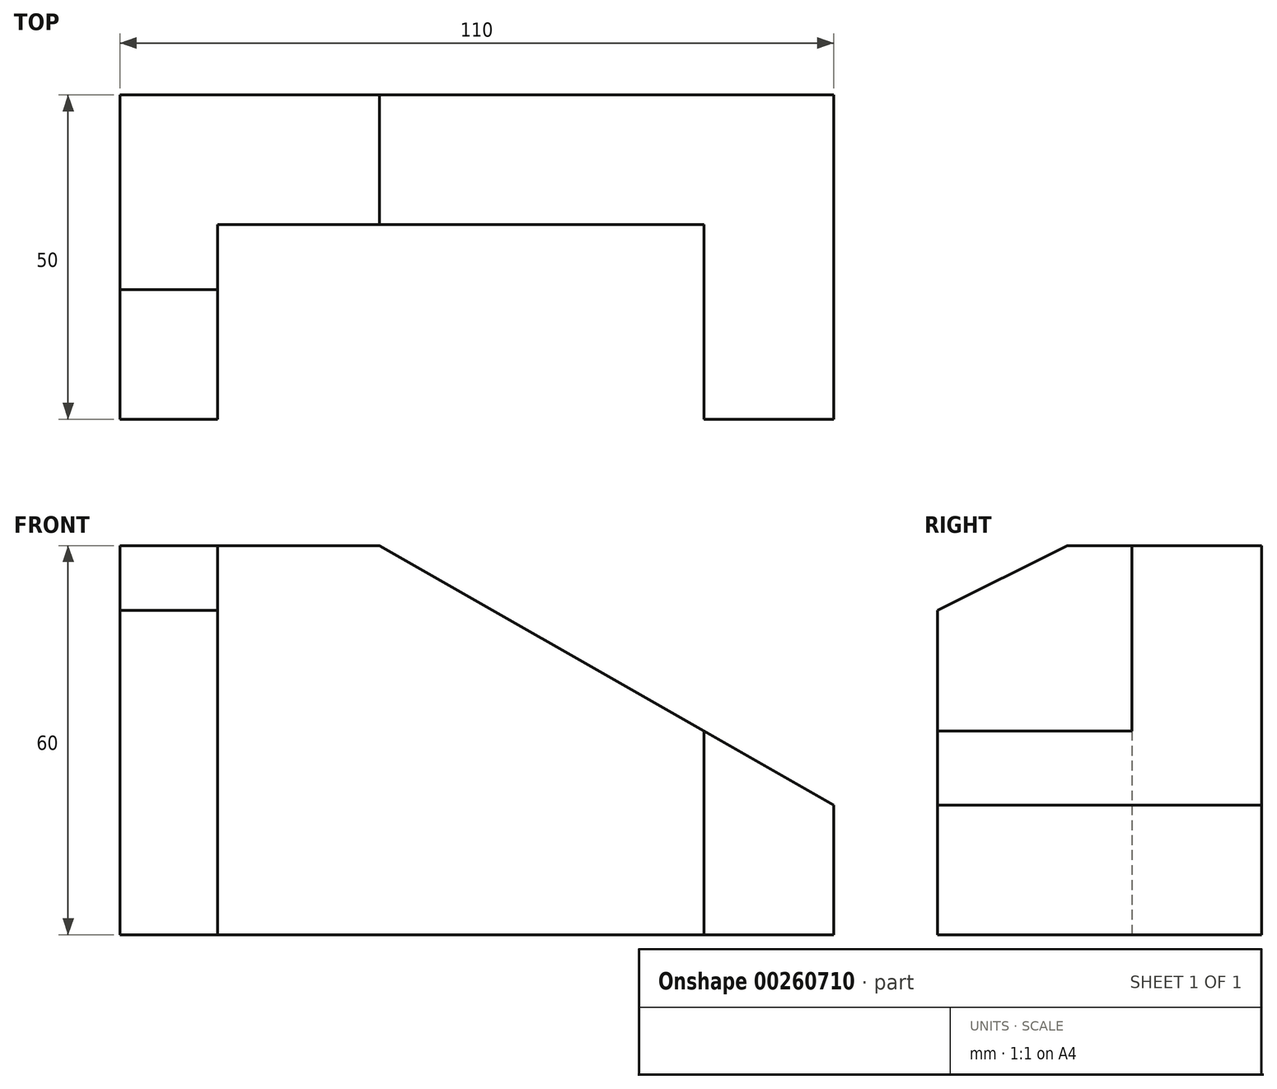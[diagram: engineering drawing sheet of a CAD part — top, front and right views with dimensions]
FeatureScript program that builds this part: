
annotation { "Feature Type Name" : "Feature", "Feature Type Description" : "" }
export const myFeature = defineFeature(function(context is Context, id is Id, definition is map)
    precondition{}
    {
        {
            assignVariable(context, id + "F0", {"name" : "B", "anyValue" : 60});
        }
        {
            var Q0;
            Q0=qCreatedBy(makeId("Top.planeOp"),FACE);
            var sketch = newSketch(context, id + "F1", { "sketchPlane" : qUnion([Q0])});
            skLineSegment(sketch, "E0", {"start": v(0, 0) * mm, "end": v(0, 50) * mm});
            skLineSegment(sketch, "E1", {"start": v(0, 50) * mm, "end": v(110, 50) * mm});
            skLineSegment(sketch, "E2", {"start": v(110, 50) * mm, "end": v(110, 0) * mm});
            skLineSegment(sketch, "E3", {"start": v(110, 0) * mm, "end": v(90, 0) * mm});
            skLineSegment(sketch, "E4", {"start": v(90, 0) * mm, "end": v(90, 30) * mm});
            skLineSegment(sketch, "E5", {"start": v(90, 30) * mm, "end": v(15, 30) * mm});
            skLineSegment(sketch, "E6", {"start": v(15, 30) * mm, "end": v(15, 0) * mm});
            skLineSegment(sketch, "E7", {"start": v(15, 0) * mm, "end": v(0, 0) * mm});
            skSolve(sketch);
        }
        {
            var Q0;
            Q0=makeQuery(id+"F1.imprint","IMPRINT",FACE,{"disambiguationData":[TD([[makeQuery(id+"F1.imprint","IMPRINT",EDGE,{"derivedFrom":sQuery(id+"F1.wireOp",EDGE,"E0")}),-1.0]])]});
            var Q1;
            Q1 = qSketchRegion(id + "F3", true);
            extrude(context, id + "F2", {"entities" : qUnion([Q0, Q1]), "depth" : (getVariable(context, 'B')) * mm});
        }
        {
            var Q0;
            Q0=makeQuery(id+"F2.opExtrude","SWEPT_FACE",FACE,{"disambiguationData":[OSD([sQuery(id+"F1.wireOp",EDGE,"E0")])]});
            var sketch = newSketch(context, id + "F3", { "sketchPlane" : qUnion([Q0])});
            skLineSegment(sketch, "E8", {"start": v(0, 60) * mm, "end": v(-20, 60) * mm});
            skLineSegment(sketch, "E9", {"start": v(-20, 60) * mm, "end": v(0, 50) * mm});
            skLineSegment(sketch, "E10", {"start": v(0, 50) * mm, "end": v(0, 60) * mm});
            skSolve(sketch);
        }
        {
            var Q0;
            Q0=makeQuery(id+"F3.imprint","IMPRINT",FACE,{"disambiguationData":[TD([[makeQuery(id+"F3.imprint","IMPRINT",EDGE,{"derivedFrom":sQuery(id+"F3.wireOp",EDGE,"E8")}),1.0]])]});
            extrude(context, id + "F4", {"entities" : qUnion([Q0]), "operationType" : NewBodyOperationType.REMOVE, "oppositeDirection" : true, "depth" : 15 * mm});
        }
        {
            var Q0;
            Q0=makeQuery(id+"F2.opExtrude","SWEPT_FACE",FACE,{"disambiguationData":[OSD([sQuery(id+"F1.wireOp",EDGE,"E1")])]});
            var sketch = newSketch(context, id + "F5", { "sketchPlane" : qUnion([Q0])});
            skLineSegment(sketch, "E11", {"start": v(-40, 60) * mm, "end": v(-110, 20) * mm});
            skLineSegment(sketch, "E12", {"start": v(-110, 20) * mm, "end": v(-110, 60) * mm});
            skLineSegment(sketch, "E13", {"start": v(-110, 60) * mm, "end": v(-40, 60) * mm});
            skSolve(sketch);
        }
        {
            var Q0;
            Q0=makeQuery(id+"F5.imprint","IMPRINT",FACE,{"disambiguationData":[TD([[makeQuery(id+"F5.imprint","IMPRINT",EDGE,{"derivedFrom":sQuery(id+"F5.wireOp",EDGE,"E11")}),-1.0]])]});
            extrude(context, id + "F6", {"entities" : qUnion([Q0]), "operationType" : NewBodyOperationType.REMOVE, "oppositeDirection" : true, "depth" : 50 * mm});
        }
    });
